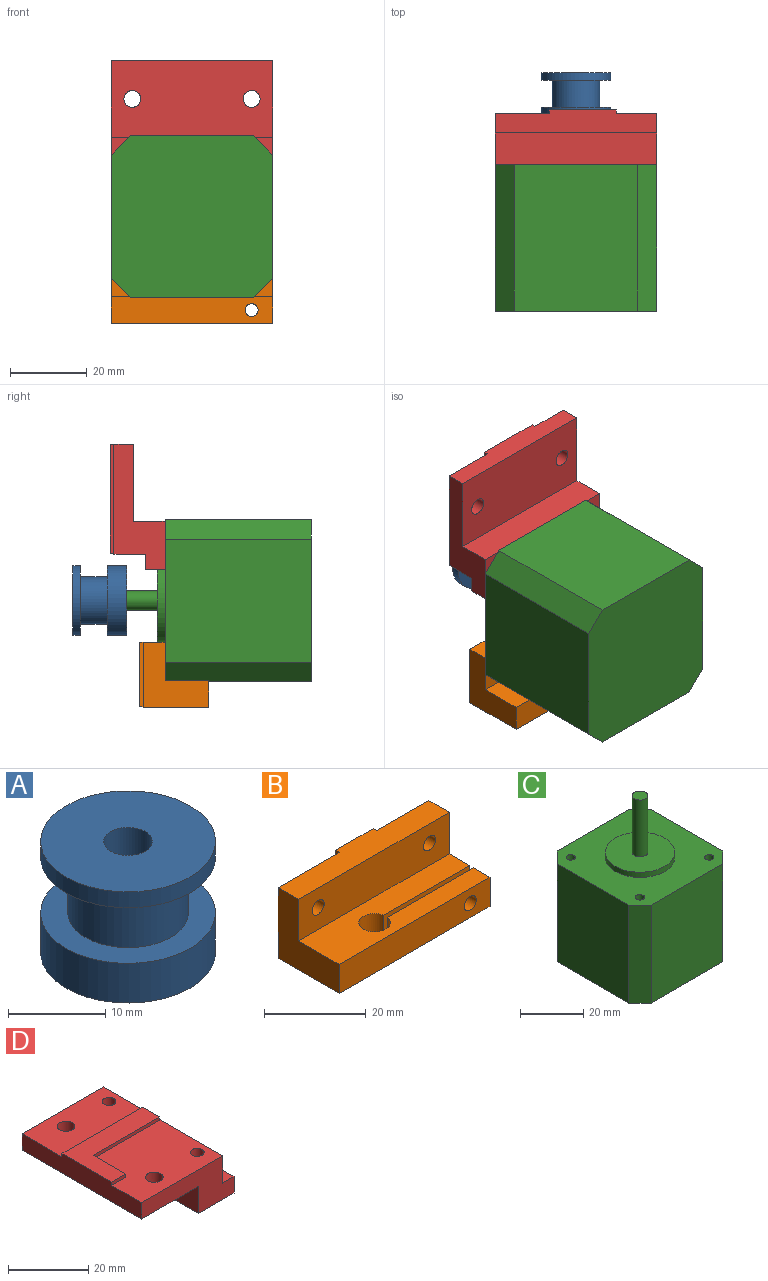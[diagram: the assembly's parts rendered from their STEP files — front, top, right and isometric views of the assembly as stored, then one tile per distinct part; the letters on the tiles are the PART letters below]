
ASSEMBLY  parts=4 mates=2
PART A: 8 faces, bbox 18x18x14 mm
  f0: cylinder r=9mm len=18mm, axis (0,0,-1), area 282.7mm2, adj f1,f2
  f1: plane 18x18mm, normal (0,0,1), area 133.7mm2, adj f0,f3
  f2: plane 18x18mm, normal (0,0,-1), area 234.8mm2, adj f0,f7
  f3: cylinder r=6.2mm len=12.4mm, axis (0,0,-1), area 272.7mm2, adj f1,f6
  f4: cylinder r=9mm len=18mm, axis (0,0,-1), area 113.1mm2, adj f5,f6
  f5: plane 18x18mm, normal (0,0,1), area 234.8mm2, adj f4,f7
  f6: plane 18x18mm, normal (0,0,-1), area 133.7mm2, adj f3,f4
  f7: cylinder r=2.5mm len=14mm, axis (0,0,1), area 219.9mm2, adj f2,f5
PART B: 22 faces, bbox 42x18x17 mm
  f0: plane 42x17mm, normal (0,1,0), area 607.1mm2, adj f3,f5,f7,f8,f10,f11,f12,f16
  f1: plane 7x4.6mm, normal (1,0,0), area 32.2mm2, adj f2,f3,f6,f14
  f2: plane 42x11.33mm, normal (0,0,1), area 421.6mm2, adj f1,f5,f6,f7,f9,f13,f14,f15
  f3: plane 42x17mm, normal (0,0,-1), area 659.9mm2, adj f0,f1,f5,f6,f7,f13,f14,f15
  f4: cylinder r=1.68mm len=4.6mm, axis (0,1,0), area 48.4mm2, adj f6,f14
  f5: plane 17x17mm, normal (-1,0,0), area 175.7mm2, adj f0,f2,f3,f6,f9,f10
  f6: plane 42x7mm, normal (0,-1,0), area 285.2mm2, adj f1,f2,f3,f4,f5
  f7: plane 17x11.4mm, normal (1,0,0), area 136.5mm2, adj f0,f2,f3,f9,f10,f15
  f8: cylinder r=1.68mm len=11.4mm, axis (0,1,0), area 120mm2, adj f0,f15
  f9: plane 42x10mm, normal (0,-1,0), area 402.4mm2, adj f2,f5,f7,f10,f11,f12
  f10: plane 42x6.67mm, normal (0,0,1), area 248.7mm2, adj f0,f5,f7,f9,f16,f17,f21
  f11: cylinder r=1.68mm len=5.67mm, axis (0,1,0), area 59.7mm2, adj f0,f9
  f12: cylinder r=1.68mm len=5.67mm, axis (0,1,0), area 59.7mm2, adj f0,f9
  f13: cylinder r=3.1mm len=7mm, axis (0,0,1), area 129.3mm2, adj f2,f3,f14,f15
  f14: plane 23.94x7mm, normal (0,1,0), area 158.8mm2, adj f1,f2,f3,f4,f13
  f15: plane 23.94x7mm, normal (0,-1,0), area 158.8mm2, adj f2,f3,f7,f8,f13
  f16: plane 16.86x1mm, normal (-1,0,0), area 16.9mm2, adj f0,f10,f20,f21
  f17: plane 2.95x1mm, normal (1,0,0), area 3mm2, adj f0,f10,f18,f21
  f18: plane 6.84x1mm, normal (0,0,-1), area 6.8mm2, adj f0,f17,f19,f21
  f19: plane 13.9x1mm, normal (1,0,0), area 13.9mm2, adj f0,f18,f20,f21
  f20: plane 3.58x1mm, normal (0,0,-1), area 3.6mm2, adj f0,f16,f19,f21
  f21: plane 16.86x10.41mm, normal (0,1,0), area 80.4mm2, adj f10,f16,f17,f18,f19,f20
PART C: 22 faces, bbox 42x42x62 mm
  f0: plane 38x32mm, normal (-1,0,0), area 1216mm2, adj f4,f5,f8,f9
  f1: plane 38x32mm, normal (0,-1,0), area 1216mm2, adj f4,f5,f7,f9
  f2: plane 38x32mm, normal (1,0,0), area 1216mm2, adj f4,f5,f6,f7
  f3: plane 38x32mm, normal (0,1,0), area 1216mm2, adj f4,f5,f6,f8
  f4: plane 42x42mm, normal (0,0,1), area 1305.6mm2, adj f0,f1,f2,f3,f6,f7,f8,f9
  f5: plane 42x42mm, normal (0,0,-1), area 1714mm2, adj f0,f1,f2,f3,f6,f7,f8,f9
  f6: plane 38x5mm, normal (0.71,0.71,0), area 268.7mm2, adj f2,f3,f4,f5
  f7: plane 38x5mm, normal (0.71,-0.71,0), area 268.7mm2, adj f1,f2,f4,f5
  f8: plane 38x5mm, normal (-0.71,0.71,0), area 268.7mm2, adj f0,f3,f4,f5
  f9: plane 38x5mm, normal (-0.71,-0.71,0), area 268.7mm2, adj f0,f1,f4,f5
  f10: cylinder r=11mm len=22mm, axis (0,0,-1), area 138.2mm2, adj f4,f11
  f11: plane 22x22mm, normal (0,0,1), area 360.5mm2, adj f10,f12
  f12: cylinder r=2.5mm len=22mm, axis (0,0,-1), area 345.6mm2, adj f11,f13
  f13: plane 5x5mm, normal (0,0,1), area 19.6mm2, adj f12
  f14: cylinder r=1.5mm len=25mm, axis (0,0,1), area 235.6mm2, adj f4,f15
  f15: plane 3x3mm, normal (0,0,1), area 7.1mm2, adj f14
  f16: cylinder r=1.5mm len=25mm, axis (0,0,1), area 235.6mm2, adj f4,f17
  f17: plane 3x3mm, normal (0,0,1), area 7.1mm2, adj f16
  f18: cylinder r=1.5mm len=25mm, axis (0,0,1), area 235.6mm2, adj f4,f19
  f19: plane 3x3mm, normal (0,0,1), area 7.1mm2, adj f18
  f20: cylinder r=1.5mm len=25mm, axis (0,0,1), area 235.6mm2, adj f4,f21
  f21: plane 3x3mm, normal (0,0,1), area 7.1mm2, adj f20
PART D: 22 faces, bbox 32.5x42x14.3 mm
  f0: plane 42x8.3mm, normal (-1,0,0), area 348.6mm2, adj f4,f7,f8,f12
  f1: plane 13.56x5mm, normal (1,0,0), area 67.8mm2, adj f4,f6,f7,f10
  f2: plane 42x8.3mm, normal (1,0,0), area 348.6mm2, adj f3,f6,f7,f8
  f3: plane 42x28.5mm, normal (0,0,1), area 922.4mm2, adj f2,f7,f8,f9,f11,f13,f14,f15
  f4: plane 42x12.5mm, normal (0,0,-1), area 477.2mm2, adj f0,f1,f5,f7,f8,f9,f10,f11
  f5: plane 13.56x5mm, normal (1,0,0), area 67.8mm2, adj f4,f6,f8,f10
  f6: plane 42x4mm, normal (0,0,1), area 138.4mm2, adj f1,f2,f5,f7,f8,f10
  f7: plane 32.5x13.3mm, normal (0,1,0), area 233mm2, adj f0,f1,f2,f3,f4,f6,f12,f13
  f8: plane 32.5x13.3mm, normal (0,-1,0), area 233mm2, adj f0,f2,f3,f4,f5,f6,f12,f13
  f9: cylinder r=1.7mm len=13.3mm, axis (0,0,-1), area 142.1mm2, adj f3,f4
  f10: cylinder r=11mm len=14.89mm, axis (0,0,-1), area 81.7mm2, adj f1,f4,f5,f6
  f11: cylinder r=1.7mm len=13.3mm, axis (0,0,-1), area 142.1mm2, adj f3,f4
  f12: plane 42x20mm, normal (0,0,-1), area 809.6mm2, adj f0,f7,f8,f13,f14,f15
  f13: plane 42x6mm, normal (-1,0,0), area 227.5mm2, adj f3,f7,f8,f12,f16,f17,f21
  f14: cylinder r=2.2mm len=5mm, axis (0,0,1), area 69.1mm2, adj f3,f12
  f15: cylinder r=2.2mm len=5mm, axis (0,0,1), area 69.1mm2, adj f3,f12
  f16: plane 28.26x1mm, normal (0,1,0), area 28.3mm2, adj f3,f13,f20,f21
  f17: plane 4.95x1mm, normal (0,-1,0), area 4.9mm2, adj f3,f13,f18,f21
  f18: plane 11.46x1mm, normal (1,0,0), area 11.5mm2, adj f3,f17,f19,f21
  f19: plane 23.31x1mm, normal (0,-1,0), area 23.3mm2, adj f3,f18,f20,f21
  f20: plane 5.99x1mm, normal (1,0,0), area 6mm2, adj f3,f16,f19,f21
  f21: plane 28.26x17.45mm, normal (0,0,1), area 226.1mm2, adj f13,f16,f17,f18,f19,f20
PLACE A rot(axis=(-1,0,0),90deg) t=(11.8,9.95,4.27)mm
PLACE B t=(-9.2,-11.38,-23.56)mm
PLACE C rot(axis=(-1,0,0),90deg) t=(-9.2,-38.05,25.27)mm
PLACE D rot(axis=(-0.58,0.58,0.58),120deg) t=(32.8,-0.05,24.87)mm
MATE fastened A.f0 <-> C.f10  axis (0,1,0) through (11.8,23.95,4.27)mm
MATE fastened D.f9 <-> C.f14  axis (0,-1,0) through (-3.7,-0.05,19.77)mm
